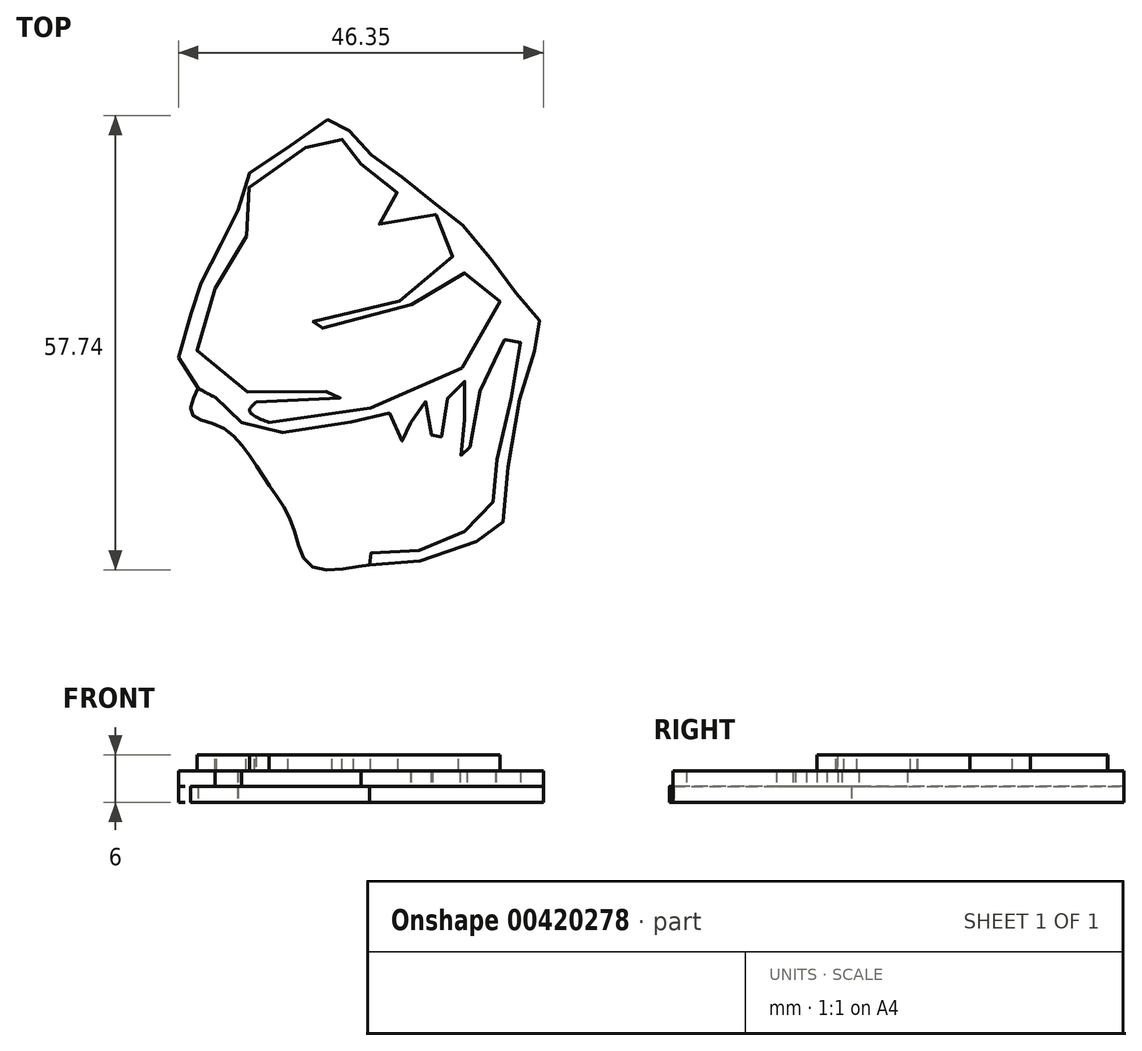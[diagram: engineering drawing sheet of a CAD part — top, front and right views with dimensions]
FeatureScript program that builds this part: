
annotation { "Feature Type Name" : "Feature", "Feature Type Description" : "" }
export const myFeature = defineFeature(function(context is Context, id is Id, definition is map)
    precondition{}
    {
        {
            var Q0;
            Q0=qCreatedBy(makeId("Top.planeOp"),FACE);
            var sketch = newSketch(context, id + "F0", { "sketchPlane" : qUnion([Q0])});
            skFitSpline(sketch, "E0", {"points": [v(1.05, -26.04) * mm, v(2.05, -26.8) * mm, v(4.9, -26.8) * mm, v(9.3, -26.07) * mm, v(14.29, -24.34) * mm, v(16.88, -23.3) * mm, v(17.92, -22.85) * mm, v(18.9, -21.62) * mm, v(19.31, -18.14) * mm, v(19.79, -13.18) * mm, v(20.93, -6.54) * mm, v(22.11, -2.42) * mm, v(23.01, 0.35) * mm, v(23.97, 2.57) * mm, v(24.1, 3.51) * mm, v(23.52, 4.4) * mm, v(21.83, 5.58) * mm, v(21.02, 6.6) * mm, v(20.08, 9.79) * mm, v(18.61, 11.6) * mm, v(16.12, 12.74) * mm, v(14.35, 15.13) * mm, v(13.53, 17.21) * mm, v(12.12, 18.58) * mm, v(9.94, 19.41) * mm, v(7.67, 21.05) * mm, v(6.45, 22.08) * mm, v(5.32, 23.92) * mm, v(3.46, 25.13) * mm, v(1.58, 25.45) * mm, v(0.4, 26.29) * mm, v(-0.3, 27.92) * mm, v(-1.42, 29.77) * mm, v(-1.96, 30.25) * mm, v(-2.98, 30.14) * mm, v(-3.64, 29.07) * mm, v(-5.5, 27.59) * mm, v(-10.06, 25.63) * mm, v(-12.13, 24.17) * mm, v(-14.32, 21.55) * mm, v(-14.7, 20.1) * mm, v(-14.66, 17.8) * mm, v(-14.92, 16.68) * mm, v(-16.33, 14.58) * mm, v(-18.25, 12.19) * mm, v(-19.12, 10.04) * mm, v(-19.62, 7.15) * mm, v(-19.68, 6.17) * mm, v(-19.87, 6.06) * mm, v(-21.45, 3.56) * mm, v(-22.08, 0.97) * mm, v(-22.22, -1.22) * mm, v(-21.62, -2.88) * mm, v(-19.74, -4.3) * mm, v(-17.6, -5.47) * mm, v(-15.53, -6.07) * mm, v(-12.36, -6.05) * mm, v(-7.18, -6.24) * mm, v(-3.38, -6) * mm, v(-1.35, -5.45) * mm, v(-0.21, -4.67) * mm, v(0, -3.6) * mm, v(0, -3.62) * mm, v(-0.57, -3.8) * mm, v(-2.54, -4.54) * mm, v(-5.53, -4.92) * mm, v(-8.55, -5.14) * mm, v(-12.46, -5.05) * mm, v(-15.57, -4.02) * mm, v(-17.24, -3.35) * mm, v(-19.5, -0.94) * mm, v(-19.88, 1.16) * mm, v(-19.43, 3.1) * mm, v(-17.48, 6.66) * mm, v(-17.51, 7.91) * mm, v(-17.53, 9.7) * mm, v(-17, 11.47) * mm, v(-15.41, 13.43) * mm, v(-13.49, 15.1) * mm, v(-12.64, 16.17) * mm, v(-12.8, 17.74) * mm, v(-13.44, 18.61) * mm, v(-13.5, 20.33) * mm, v(-12.15, 22.9) * mm, v(-10.21, 24.4) * mm, v(-7.75, 25.53) * mm, v(-5.16, 26.69) * mm, v(-3.75, 27.47) * mm, v(-2.88, 28.25) * mm, v(-2.7, 28.25) * mm, v(-2.19, 28.25) * mm, v(-1.5, 27.6) * mm, v(-1.74, 26.26) * mm, v(-2.7, 25.4) * mm, v(-2.66, 25.24) * mm, v(-2.55, 24.63) * mm, v(-0.31, 24.16) * mm, v(2.37, 24.05) * mm, v(3.98, 23.51) * mm, v(5.1, 22.62) * mm, v(5.61, 21.62) * mm, v(5.45, 20.18) * mm, v(4.23, 18.55) * mm, v(2.84, 17.21) * mm, v(2.16, 16.26) * mm, v(2.45, 16.15) * mm, v(4.77, 17.35) * mm, v(6.87, 18.14) * mm, v(8.78, 18.44) * mm, v(9.8, 18.2) * mm, v(11.64, 16.78) * mm, v(12.81, 15.78) * mm, v(13.35, 14.74) * mm, v(13.11, 13.25) * mm, v(12.52, 12.26) * mm, v(11.76, 10.74) * mm, v(10.42, 9.34) * mm, v(7.07, 7.28) * mm, v(2.2, 5.34) * mm, v(-1.56, 4.4) * mm, v(-5.89, 4.12) * mm, v(-8.32, 4.03) * mm, v(-8.23, 3.87) * mm, v(-6.83, 3.33) * mm, v(-4.4, 3.27) * mm, v(-1.45, 3.65) * mm, v(3.51, 4.8) * mm, v(8.7, 6.8) * mm, v(10.67, 7.6) * mm, v(10.87, 7.84) * mm, v(12.74, 9.53) * mm, v(14.4, 10.42) * mm, v(15.83, 10.77) * mm, v(16.09, 10.77) * mm, v(17.07, 10.17) * mm, v(18.36, 8.07) * mm, v(18.57, 5.29) * mm, v(17.86, 2.77) * mm, v(15.29, -0.47) * mm, v(11.4, -3.34) * mm, v(5.64, -5.79) * mm, v(1.04, -7.14) * mm, v(-4.38, -8.2) * mm, v(-10.73, -8.68) * mm, v(-14.18, -8.68) * mm, v(-14.21, -8.76) * mm, v(-11.87, -9.7) * mm, v(-6.45, -9.77) * mm, v(1.15, -8.23) * mm, v(3.86, -7.46) * mm, v(4.5, -7.46) * mm, v(5.06, -8.05) * mm, v(5.53, -10.01) * mm, v(6.33, -11.2) * mm, v(6.81, -11.42) * mm, v(7.2, -10.76) * mm, v(7.26, -8.63) * mm, v(7.4, -7.6) * mm, v(8.3, -6.45) * mm, v(9.33, -6.03) * mm, v(9.9, -6.43) * mm, v(9.97, -9.53) * mm, v(9.9, -11.24) * mm, v(9.97, -11.55) * mm, v(10.26, -11.74) * mm, v(11.33, -10.17) * mm, v(11.8, -8.44) * mm, v(11.97, -5.52) * mm, v(12.58, -4.06) * mm, v(13.24, -3.37) * mm, v(14.2, -3.53) * mm, v(14.41, -5.28) * mm, v(14.1, -8.29) * mm, v(13.75, -10.38) * mm, v(13.56, -12.46) * mm, v(13.9, -13.6) * mm, v(14.01, -13.84) * mm, v(14.33, -13.57) * mm, v(14.86, -11.18) * mm, v(15.69, -6.19) * mm, v(17.63, -0.71) * mm, v(19.75, 2.4) * mm, v(20.66, 2.8) * mm, v(21.13, 2.66) * mm, v(21.13, 0.75) * mm, v(20.31, -4.54) * mm, v(18.8, -10.36) * mm, v(18.08, -15.78) * mm, v(18, -18.03) * mm, v(17.04, -19.9) * mm, v(15.2, -21.8) * mm, v(11.93, -23.7) * mm, v(8.32, -24.92) * mm, v(3.99, -25.24) * mm, v(1.76, -25.24) * mm, v(1.01, -25.4) * mm, v(1.05, -26.04) * mm]});
            skFitSpline(sketch, "E1", {"points": [v(-19.74, -4.3) * mm, v(-20.56, -7.55) * mm, v(-17.18, -9.05) * mm, v(-13.34, -12.67) * mm, v(-10.6, -16.81) * mm, v(-7.76, -21.66) * mm, v(-5, -27.11) * mm, v(2.05, -26.8) * mm], "startDerivative": vector(-11.32, -25.53) * mm, "endDerivative": vector(21.95, -0.55) * mm});
            skLineSegment(sketch, "E2", {"start": v(-14.18, -8.68) * mm, "end": v(-17.6, -5.47) * mm});
            skFitSpline(sketch, "E3", {"points": [v(-12.36, -6.05) * mm, v(-13.17, -7.24) * mm, v(-10.73, -8.68) * mm], "startDerivative": vector(-3.22, -2.93) * mm, "endDerivative": vector(5.97, -2.37) * mm});
            skSolve(sketch);
        }
        {
            var Q0;
            {var subQ0=sQuery(id+"F0.wireOp",EDGE,"E2");Q0=makeQuery(id+"F0.imprint","IMPRINT",FACE,{"disambiguationData":[TD([[makeQuery(id+"F0.imprint","IMPRINT",EDGE,{"derivedFrom":subQ0}),-1.0]])]});}
            var Q1;
            {var subQ0=sQuery(id+"F0.wireOp",EDGE,"E1");var subQ1=sQuery(id+"F0.wireOp",EDGE,"E0");var subQ2=makeQuery(id+"F0.imprint","INTERSECT",VERTEX,{"disambiguationData":[OD(0.0)],"derivedFrom":[subQ1,subQ0]});Q1=makeQuery(id+"F0.imprint","IMPRINT",FACE,{"disambiguationData":[TD([[makeQuery(id+"F0.imprint","IMPRINT",EDGE,{"disambiguationData":[TD([[subQ2,1.0]])],"derivedFrom":subQ1}),1.0]])]});}
            var Q2;
            {var subQ0=sQuery(id+"F0.wireOp",EDGE,"E1");Q2=makeQuery(id+"F0.imprint","IMPRINT",FACE,{"disambiguationData":[TD([[makeQuery(id+"F0.imprint","IMPRINT",EDGE,{"derivedFrom":subQ0}),1.0]])]});}
            var Q3;
            {var subQ0=sQuery(id+"F0.wireOp",EDGE,"E3");Q3=makeQuery(id+"F0.imprint","IMPRINT",FACE,{"disambiguationData":[TD([[makeQuery(id+"F0.imprint","IMPRINT",EDGE,{"derivedFrom":subQ0}),1.0]])]});}
            extrude(context, id + "F1", {"entities" : qUnion([Q0, Q1, Q2, Q3]), "depth" : 2 * mm});
        }
        {
            var Q0;
            {var subQ0=sQuery(id+"F0.wireOp",EDGE,"E1");var subQ1=sQuery(id+"F0.wireOp",EDGE,"E0");var subQ2=makeQuery(id+"F0.imprint","INTERSECT",VERTEX,{"disambiguationData":[OD(0.0)],"derivedFrom":[subQ1,subQ0]});Q0=makeQuery(id+"F0.imprint","IMPRINT",FACE,{"disambiguationData":[TD([[makeQuery(id+"F0.imprint","IMPRINT",EDGE,{"disambiguationData":[TD([[subQ2,1.0]])],"derivedFrom":subQ1}),1.0]])]});}
            var Q1;
            {var subQ0=sQuery(id+"F0.wireOp",EDGE,"E2");Q1=makeQuery(id+"F0.imprint","IMPRINT",FACE,{"disambiguationData":[TD([[makeQuery(id+"F0.imprint","IMPRINT",EDGE,{"derivedFrom":subQ0}),-1.0]])]});}
            var Q2;
            {var subQ0=sQuery(id+"F0.wireOp",EDGE,"E3");Q2=makeQuery(id+"F0.imprint","IMPRINT",FACE,{"disambiguationData":[TD([[makeQuery(id+"F0.imprint","IMPRINT",EDGE,{"derivedFrom":subQ0}),1.0]])]});}
            extrude(context, id + "F2", {"entities" : qUnion([Q0, Q1, Q2]), "depth" : 4 * mm, "hasSecondDirection" : true, "secondDirectionOppositeDirection" : true, "secondDirectionDepth" : -2 * mm});
        }
        {
            var Q0;
            {var subQ0=sQuery(id+"F0.wireOp",EDGE,"E3");Q0=makeQuery(id+"F0.imprint","IMPRINT",FACE,{"disambiguationData":[TD([[makeQuery(id+"F0.imprint","IMPRINT",EDGE,{"derivedFrom":subQ0}),1.0]])]});}
            extrude(context, id + "F3", {"entities" : qUnion([Q0]), "depth" : 6 * mm, "hasSecondDirection" : true, "secondDirectionOppositeDirection" : true, "secondDirectionDepth" : -4 * mm});
        }
    });
